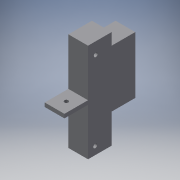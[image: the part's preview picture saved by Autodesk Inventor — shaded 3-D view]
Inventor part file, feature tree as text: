
AUTODESK INVENTOR PART (.ipt)
format: ipt  version: 2019.4 (Build 234330000, 330)  size: 123,392 bytes
history: native  units: mm
features: extrude x2, sketch x2, projected_geometry x1
ambient origin geometry x8: Origin, YZ Plane, XZ Plane, XY Plane, X Axis, Y Axis, Z Axis, Center Point
bodies: Solid1 (feature_tree)
feature tree (5):
  extrude  "Extrusion1"  Depth=6.0mm
  extrude  "Extrusion2"  Depth=1.0mm
  sketch  "Sketch1"  dims[d0=25.0mm d1=6.0mm]
  sketch  "Sketch2"  dims[d2=1.0mm d3=1.0mm d4=20.0mm d5=14.5mm d6=6.0mm d7=7.5mm d8=1.0mm d9=6.0mm d10=10.0mm d11=5.0mm d12=0.0mm d13=2.0mm d14=1.0mm d15=5.0mm d16=0.0mm]
  projected_geometry  "Projected Loop1"
